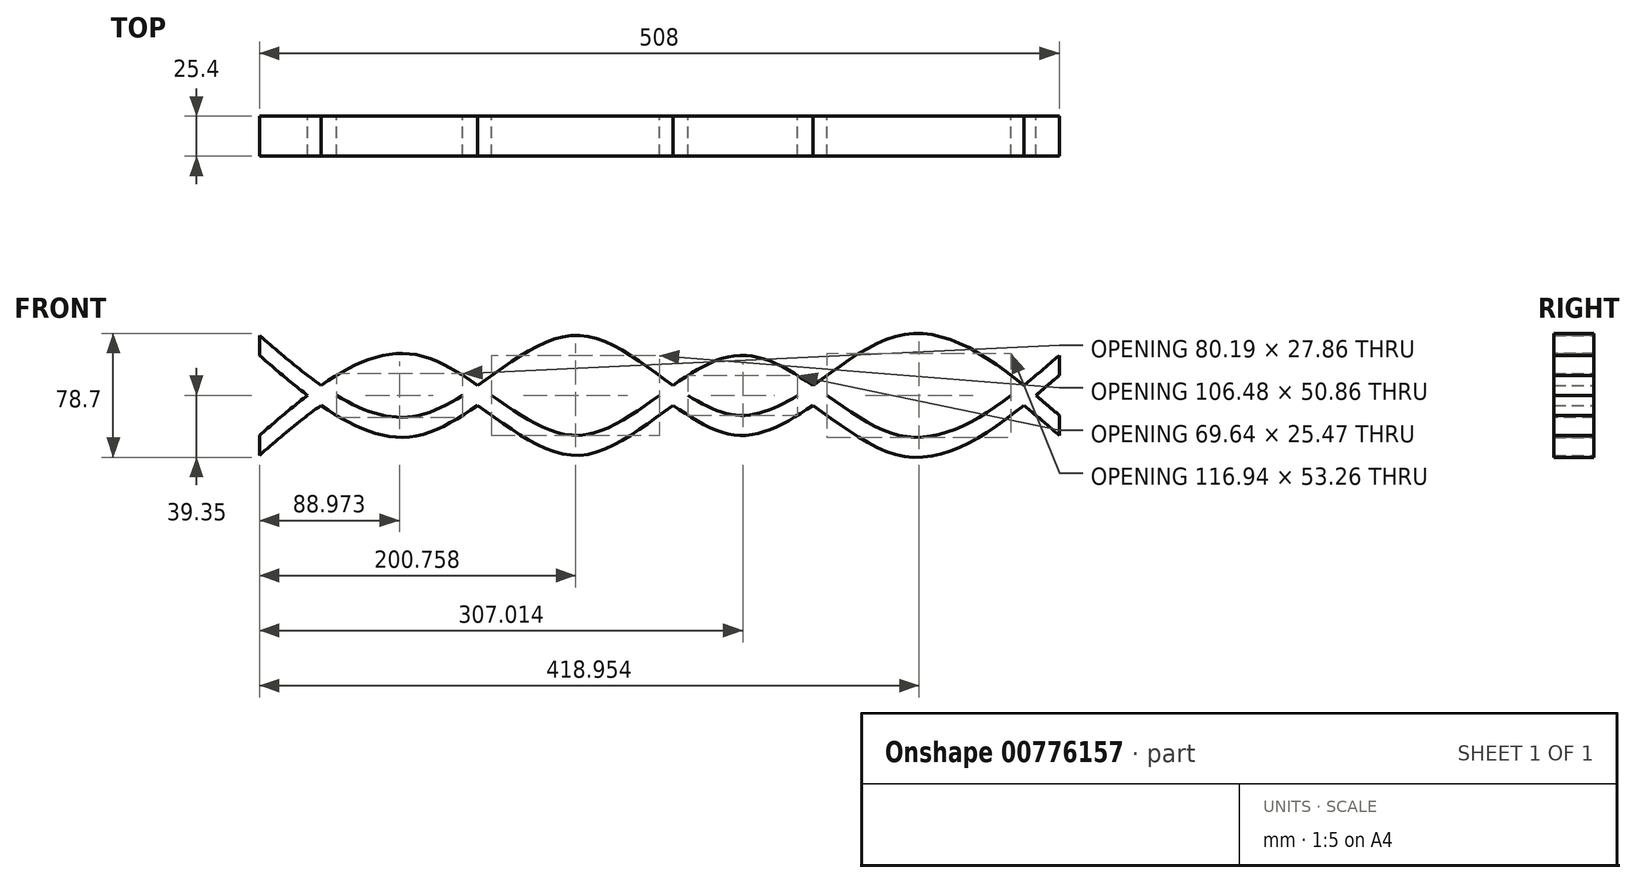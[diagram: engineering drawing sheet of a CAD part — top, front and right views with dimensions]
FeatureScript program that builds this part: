
annotation { "Feature Type Name" : "Feature", "Feature Type Description" : "" }
export const myFeature = defineFeature(function(context is Context, id is Id, definition is map)
    precondition{}
    {
        {
            var Q0;
            Q0=qCreatedBy(makeId("Front.planeOp"),FACE);
            var sketch = newSketch(context, id + "F0", { "sketchPlane" : qUnion([Q0])});
            skFitSpline(sketch, "E0", {"points": [v(-254, -25.4) * mm, v(-152.4, 25.4) * mm, v(-50.8, -25.4) * mm, v(50.8, 25.4) * mm, v(152.4, -25.4) * mm, v(254, 25.4) * mm], "startDerivative": vector(508, 438.73) * mm, "endDerivative": vector(508, 438.73) * mm});
            skFitSpline(sketch, "E1", {"points": [v(-254, -38.1) * mm, v(-152.4, 12.7) * mm, v(-50.8, -38.1) * mm, v(50.8, 12.7) * mm, v(152.4, -38.1) * mm, v(254, 12.7) * mm], "startDerivative": vector(508, 438.73) * mm, "endDerivative": vector(508, 438.73) * mm});
            skLineSegment(sketch, "E2", {"start": v(254, 25.4) * mm, "end": v(254, 12.7) * mm});
            skLineSegment(sketch, "E3", {"start": v(-254, -25.4) * mm, "end": v(-254, -38.1) * mm});
            skFitSpline(sketch, "E4.MirrorCS", {"points": [v(-254, 25.4) * mm, v(-152.4, -25.4) * mm, v(-50.8, 25.4) * mm, v(50.8, -25.4) * mm, v(152.4, 25.4) * mm, v(254, -25.4) * mm], "startDerivative": vector(508, -438.73) * mm, "endDerivative": vector(508, -438.73) * mm});
            skFitSpline(sketch, "E5.MirrorCS", {"points": [v(-254, 38.1) * mm, v(-152.4, -12.7) * mm, v(-50.8, 38.1) * mm, v(50.8, -12.7) * mm, v(152.4, 38.1) * mm, v(254, -12.7) * mm], "startDerivative": vector(508, -438.73) * mm, "endDerivative": vector(508, -438.73) * mm});
            skLineSegment(sketch, "E6", {"start": v(-254, 25.4) * mm, "end": v(-254, 38.1) * mm});
            skLineSegment(sketch, "E7", {"start": v(254, -12.7) * mm, "end": v(254, -25.4) * mm});
            skSolve(sketch);
        }
        {
            var Q0;
            {var subQ0=sQuery(id+"F0.wireOp",EDGE,"E4.MirrorCS");var subQ1=sQuery(id+"F0.wireOp",EDGE,"E1");var subQ2=makeQuery(id+"F0.imprint","INTERSECT",VERTEX,{"disambiguationData":[OD(0.0)],"derivedFrom":[subQ1,subQ0]});Q0=makeQuery(id+"F0.imprint","IMPRINT",FACE,{"disambiguationData":[TD([[makeQuery(id+"F0.imprint","IMPRINT",EDGE,{"disambiguationData":[TD([[subQ2,-1.0]])],"derivedFrom":subQ1}),-1.0]])]});}
            var Q1;
            {var subQ0=sQuery(id+"F0.wireOp",EDGE,"E5.MirrorCS");var subQ1=sQuery(id+"F0.wireOp",EDGE,"E0");var subQ2=makeQuery(id+"F0.imprint","INTERSECT",VERTEX,{"disambiguationData":[OD(0.0)],"derivedFrom":[subQ1,subQ0]});Q1=makeQuery(id+"F0.imprint","IMPRINT",FACE,{"disambiguationData":[TD([[makeQuery(id+"F0.imprint","IMPRINT",EDGE,{"disambiguationData":[TD([[subQ2,-1.0]])],"derivedFrom":subQ1}),-1.0]])]});}
            var Q2;
            {var subQ0=sQuery(id+"F0.wireOp",EDGE,"E4.MirrorCS");var subQ1=sQuery(id+"F0.wireOp",EDGE,"E0");var subQ2=makeQuery(id+"F0.imprint","INTERSECT",VERTEX,{"disambiguationData":[OD(0.0)],"derivedFrom":[subQ1,subQ0]});Q2=makeQuery(id+"F0.imprint","IMPRINT",FACE,{"disambiguationData":[TD([[makeQuery(id+"F0.imprint","IMPRINT",EDGE,{"disambiguationData":[TD([[subQ2,-1.0]])],"derivedFrom":subQ1}),-1.0]])]});}
            var Q3;
            {var subQ0=sQuery(id+"F0.wireOp",EDGE,"E3");Q3=makeQuery(id+"F0.imprint","IMPRINT",FACE,{"disambiguationData":[TD([[makeQuery(id+"F0.imprint","IMPRINT",EDGE,{"derivedFrom":subQ0}),1.0]])]});}
            var Q4;
            {var subQ5=sQuery(id+"F0.wireOp",EDGE,"E6");Q4=makeQuery(id+"F0.imprint","IMPRINT",FACE,{"disambiguationData":[TD([[makeQuery(id+"F0.imprint","IMPRINT",EDGE,{"derivedFrom":subQ5}),-1.0]])]});}
            var Q5;
            {var subQ0=sQuery(id+"F0.wireOp",EDGE,"E4.MirrorCS");var subQ1=sQuery(id+"F0.wireOp",EDGE,"E0");var subQ2=makeQuery(id+"F0.imprint","INTERSECT",VERTEX,{"disambiguationData":[OD(1.0)],"derivedFrom":[subQ1,subQ0]});Q5=makeQuery(id+"F0.imprint","IMPRINT",FACE,{"disambiguationData":[TD([[makeQuery(id+"F0.imprint","IMPRINT",EDGE,{"disambiguationData":[TD([[subQ2,-1.0]])],"derivedFrom":subQ1}),-1.0]])]});}
            var Q6;
            {var subQ0=sQuery(id+"F0.wireOp",EDGE,"E5.MirrorCS");var subQ1=sQuery(id+"F0.wireOp",EDGE,"E0");var subQ2=makeQuery(id+"F0.imprint","INTERSECT",VERTEX,{"disambiguationData":[OD(1.0)],"derivedFrom":[subQ1,subQ0]});Q6=makeQuery(id+"F0.imprint","IMPRINT",FACE,{"disambiguationData":[TD([[makeQuery(id+"F0.imprint","IMPRINT",EDGE,{"disambiguationData":[TD([[subQ2,-1.0]])],"derivedFrom":subQ1}),-1.0]])]});}
            var Q7;
            {var subQ0=sQuery(id+"F0.wireOp",EDGE,"E5.MirrorCS");var subQ1=sQuery(id+"F0.wireOp",EDGE,"E0");var subQ2=makeQuery(id+"F0.imprint","INTERSECT",VERTEX,{"disambiguationData":[OD(1.0)],"derivedFrom":[subQ1,subQ0]});Q7=makeQuery(id+"F0.imprint","IMPRINT",FACE,{"disambiguationData":[TD([[makeQuery(id+"F0.imprint","IMPRINT",EDGE,{"disambiguationData":[TD([[subQ2,-1.0]])],"derivedFrom":subQ1}),1.0]])]});}
            var Q8;
            {var subQ0=sQuery(id+"F0.wireOp",EDGE,"E4.MirrorCS");var subQ1=sQuery(id+"F0.wireOp",EDGE,"E1");var subQ2=makeQuery(id+"F0.imprint","INTERSECT",VERTEX,{"disambiguationData":[OD(2.0)],"derivedFrom":[subQ1,subQ0]});Q8=makeQuery(id+"F0.imprint","IMPRINT",FACE,{"disambiguationData":[TD([[makeQuery(id+"F0.imprint","IMPRINT",EDGE,{"disambiguationData":[TD([[subQ2,-1.0]])],"derivedFrom":subQ1}),-1.0]])]});}
            var Q9;
            {var subQ0=sQuery(id+"F0.wireOp",EDGE,"E5.MirrorCS");var subQ1=sQuery(id+"F0.wireOp",EDGE,"E0");var subQ2=makeQuery(id+"F0.imprint","INTERSECT",VERTEX,{"disambiguationData":[OD(2.0)],"derivedFrom":[subQ1,subQ0]});Q9=makeQuery(id+"F0.imprint","IMPRINT",FACE,{"disambiguationData":[TD([[makeQuery(id+"F0.imprint","IMPRINT",EDGE,{"disambiguationData":[TD([[subQ2,-1.0]])],"derivedFrom":subQ1}),-1.0]])]});}
            var Q10;
            {var subQ0=sQuery(id+"F0.wireOp",EDGE,"E5.MirrorCS");var subQ1=sQuery(id+"F0.wireOp",EDGE,"E0");var subQ2=makeQuery(id+"F0.imprint","INTERSECT",VERTEX,{"disambiguationData":[OD(2.0)],"derivedFrom":[subQ1,subQ0]});Q10=makeQuery(id+"F0.imprint","IMPRINT",FACE,{"disambiguationData":[TD([[makeQuery(id+"F0.imprint","IMPRINT",EDGE,{"disambiguationData":[TD([[subQ2,1.0]])],"derivedFrom":subQ1}),-1.0]])]});}
            var Q11;
            {var subQ0=sQuery(id+"F0.wireOp",EDGE,"E4.MirrorCS");var subQ1=sQuery(id+"F0.wireOp",EDGE,"E0");var subQ2=makeQuery(id+"F0.imprint","INTERSECT",VERTEX,{"disambiguationData":[OD(3.0)],"derivedFrom":[subQ1,subQ0]});Q11=makeQuery(id+"F0.imprint","IMPRINT",FACE,{"disambiguationData":[TD([[makeQuery(id+"F0.imprint","IMPRINT",EDGE,{"disambiguationData":[TD([[subQ2,-1.0]])],"derivedFrom":subQ1}),-1.0]])]});}
            var Q12;
            {var subQ0=sQuery(id+"F0.wireOp",EDGE,"E5.MirrorCS");var subQ1=sQuery(id+"F0.wireOp",EDGE,"E0");var subQ2=makeQuery(id+"F0.imprint","INTERSECT",VERTEX,{"disambiguationData":[OD(3.0)],"derivedFrom":[subQ1,subQ0]});Q12=makeQuery(id+"F0.imprint","IMPRINT",FACE,{"disambiguationData":[TD([[makeQuery(id+"F0.imprint","IMPRINT",EDGE,{"disambiguationData":[TD([[subQ2,-1.0]])],"derivedFrom":subQ1}),-1.0]])]});}
            var Q13;
            {var subQ0=sQuery(id+"F0.wireOp",EDGE,"E5.MirrorCS");var subQ1=sQuery(id+"F0.wireOp",EDGE,"E0");var subQ2=makeQuery(id+"F0.imprint","INTERSECT",VERTEX,{"disambiguationData":[OD(3.0)],"derivedFrom":[subQ1,subQ0]});Q13=makeQuery(id+"F0.imprint","IMPRINT",FACE,{"disambiguationData":[TD([[makeQuery(id+"F0.imprint","IMPRINT",EDGE,{"disambiguationData":[TD([[subQ2,-1.0]])],"derivedFrom":subQ1}),1.0]])]});}
            var Q14;
            {var subQ5=sQuery(id+"F0.wireOp",EDGE,"E7");Q14=makeQuery(id+"F0.imprint","IMPRINT",FACE,{"disambiguationData":[TD([[makeQuery(id+"F0.imprint","IMPRINT",EDGE,{"derivedFrom":subQ5}),-1.0]])]});}
            var Q15;
            {var subQ0=sQuery(id+"F0.wireOp",EDGE,"E2");Q15=makeQuery(id+"F0.imprint","IMPRINT",FACE,{"disambiguationData":[TD([[makeQuery(id+"F0.imprint","IMPRINT",EDGE,{"derivedFrom":subQ0}),-1.0]])]});}
            var Q16;
            {var subQ0=sQuery(id+"F0.wireOp",EDGE,"E5.MirrorCS");var subQ1=sQuery(id+"F0.wireOp",EDGE,"E0");var subQ2=makeQuery(id+"F0.imprint","INTERSECT",VERTEX,{"disambiguationData":[OD(4.0)],"derivedFrom":[subQ1,subQ0]});Q16=makeQuery(id+"F0.imprint","IMPRINT",FACE,{"disambiguationData":[TD([[makeQuery(id+"F0.imprint","IMPRINT",EDGE,{"disambiguationData":[TD([[subQ2,1.0]])],"derivedFrom":subQ1}),-1.0]])]});}
            var Q17;
            Q17=sQuery(id+"F0.wireOp",EDGE,"E4.MirrorCS");
            var Q18;
            Q18=sQuery(id+"F0.wireOp",EDGE,"E0");
            extrude(context, id + "F1", {"entities" : qUnion([Q0, Q1, Q2, Q3, Q4, Q5, Q6, Q7, Q8, Q9, Q10, Q11, Q12, Q13, Q14, Q15, Q16]), "surfaceEntities" : qUnion([Q17, Q18]), "depth" : 25.4 * mm, "offsetDistance" : 25.4 * mm});
        }
    });
